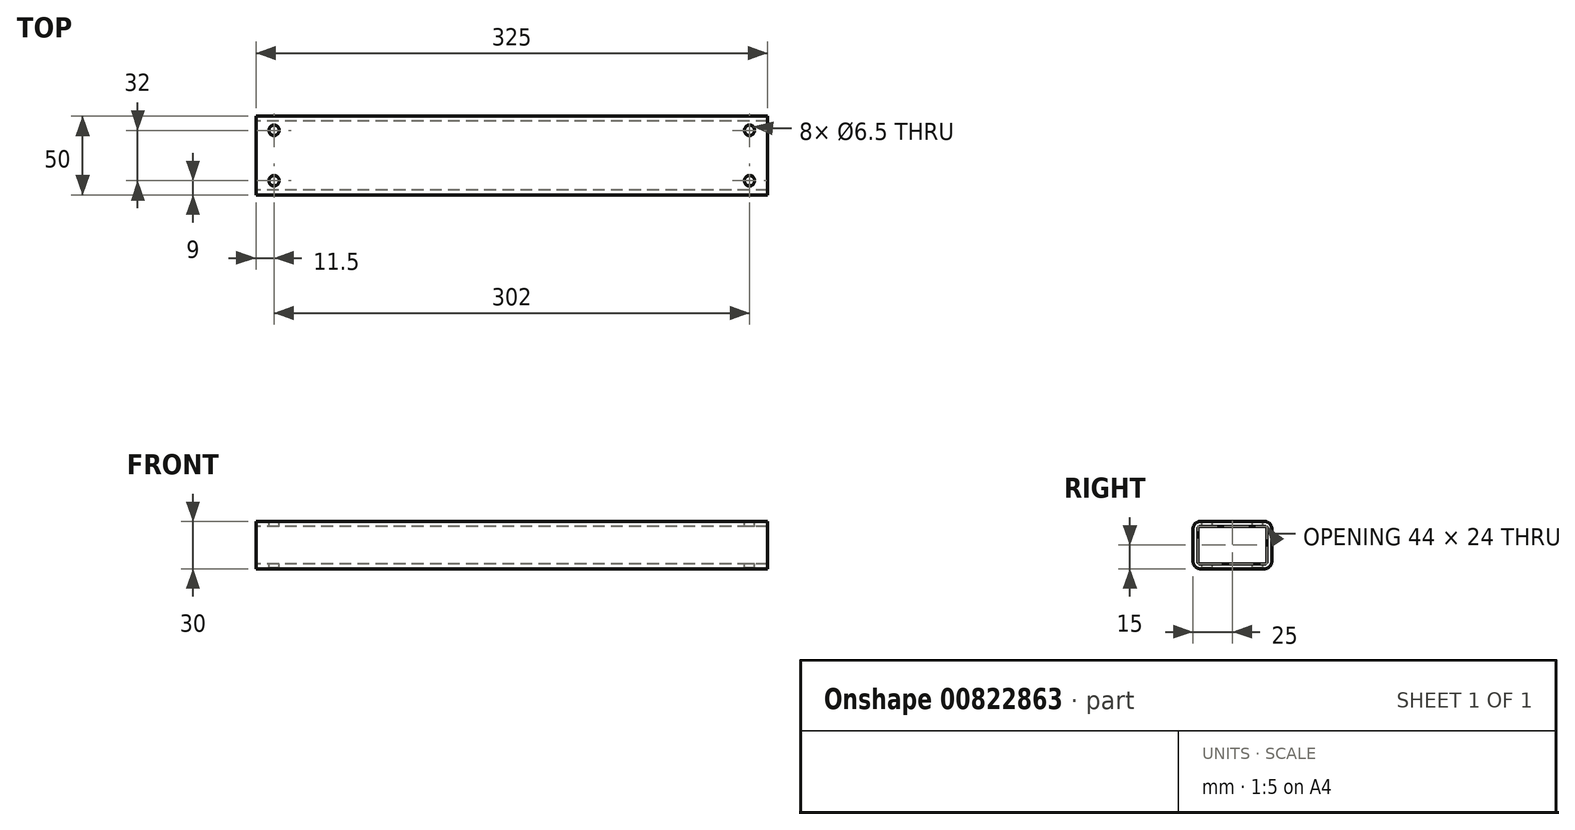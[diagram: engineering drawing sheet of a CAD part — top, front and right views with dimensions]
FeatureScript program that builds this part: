
annotation { "Feature Type Name" : "Feature", "Feature Type Description" : "" }
export const myFeature = defineFeature(function(context is Context, id is Id, definition is map)
    precondition{}
    {
        {
            var Q0;
            Q0=qCreatedBy(makeId("Right.planeOp"),FACE);
            var sketch = newSketch(context, id + "F0", { "sketchPlane" : qUnion([Q0])});
            skLineSegment(sketch, "E0.bottom", {"start": v(-25, -15) * mm, "end": v(25, -15) * mm});
            skLineSegment(sketch, "E0.top", {"start": v(-25, 15) * mm, "end": v(25, 15) * mm});
            skLineSegment(sketch, "E0.left", {"start": v(-25, -15) * mm, "end": v(-25, 15) * mm});
            skLineSegment(sketch, "E0.right", {"start": v(25, -15) * mm, "end": v(25, 15) * mm});
            skPoint(sketch, "E0.middle", {"position": v(0, 0) * mm});
            skLineSegment(sketch, "E1.0", {"start": v(-22, 12) * mm, "end": v(22, 12) * mm});
            skLineSegment(sketch, "E1.1", {"start": v(-22, -12) * mm, "end": v(-22, 12) * mm});
            skLineSegment(sketch, "E1.2", {"start": v(-22, -12) * mm, "end": v(22, -12) * mm});
            skLineSegment(sketch, "E1.3", {"start": v(22, -12) * mm, "end": v(22, 12) * mm});
            skSolve(sketch);
        }
        {
            var Q0;
            Q0=qSketchRegion(id+"F0",true);
            extrude(context, id + "F1", {"entities" : qUnion([Q0]), "endBound" : BoundingType.SYMMETRIC, "depth" : 325 * mm, "offsetDistance" : 25 * mm});
        }
        {
            var Q0;
            Q0=makeQuery(id+"F1.opExtrude","SWEPT_EDGE",EDGE,{"disambiguationData":[OSD([sQuery(id+"F0.wireOp",EDGE,"E1.1"),sQuery(id+"F0.wireOp",EDGE,"E1.2")])]});
            var Q1;
            Q1=makeQuery(id+"F1.opExtrude","SWEPT_EDGE",EDGE,{"disambiguationData":[OSD([sQuery(id+"F0.wireOp",EDGE,"E1.0"),sQuery(id+"F0.wireOp",EDGE,"E1.1")])]});
            var Q2;
            Q2=makeQuery(id+"F1.opExtrude","SWEPT_EDGE",EDGE,{"disambiguationData":[OSD([sQuery(id+"F0.wireOp",EDGE,"E1.2"),sQuery(id+"F0.wireOp",EDGE,"E1.3")])]});
            var Q3;
            Q3=makeQuery(id+"F1.opExtrude","SWEPT_EDGE",EDGE,{"disambiguationData":[OSD([sQuery(id+"F0.wireOp",EDGE,"E1.0"),sQuery(id+"F0.wireOp",EDGE,"E1.3")])]});
            fillet(context, id + "F2", {"entities" : qUnion([Q0, Q1, Q2, Q3]), "radius" : 1.5 * mm, "tangentPropagation" : true, "allowEdgeOverflow" : false});
        }
        {
            var Q0;
            Q0=makeQuery(id+"F1.opExtrude","SWEPT_EDGE",EDGE,{"disambiguationData":[OSD([sQuery(id+"F0.wireOp",EDGE,"E0.top"),sQuery(id+"F0.wireOp",EDGE,"E0.left")])]});
            var Q1;
            Q1=makeQuery(id+"F1.opExtrude","SWEPT_EDGE",EDGE,{"disambiguationData":[OSD([sQuery(id+"F0.wireOp",EDGE,"E0.bottom"),sQuery(id+"F0.wireOp",EDGE,"E0.left")])]});
            var Q2;
            Q2=makeQuery(id+"F1.opExtrude","SWEPT_EDGE",EDGE,{"disambiguationData":[OSD([sQuery(id+"F0.wireOp",EDGE,"E0.bottom"),sQuery(id+"F0.wireOp",EDGE,"E0.right")])]});
            var Q3;
            Q3=makeQuery(id+"F1.opExtrude","SWEPT_EDGE",EDGE,{"disambiguationData":[OSD([sQuery(id+"F0.wireOp",EDGE,"E0.top"),sQuery(id+"F0.wireOp",EDGE,"E0.right")])]});
            fillet(context, id + "F3", {"entities" : qUnion([Q0, Q1, Q2, Q3]), "radius" : 4.5 * mm, "tangentPropagation" : true, "allowEdgeOverflow" : false});
        }
        {
            var Q0;
            Q0=makeQuery(id+"F1.opExtrude","SWEPT_FACE",FACE,{"disambiguationData":[OSD([sQuery(id+"F0.wireOp",EDGE,"E0.top")])]});
            var sketch = newSketch(context, id + "F4", { "sketchPlane" : qUnion([Q0])});
            skLineSegment(sketch, "E2.bottom", {"start": v(-151, 16) * mm, "end": v(151, 16) * mm, "construction": true});
            skLineSegment(sketch, "E2.top", {"start": v(-151, -16) * mm, "end": v(151, -16) * mm, "construction": true});
            skLineSegment(sketch, "E2.left", {"start": v(-151, 16) * mm, "end": v(-151, -16) * mm, "construction": true});
            skLineSegment(sketch, "E2.right", {"start": v(151, 16) * mm, "end": v(151, -16) * mm, "construction": true});
            skPoint(sketch, "E2.middle", {"position": v(0, 0) * mm});
            skCircle(sketch, "E3", {"center": v(-151, 16) * mm, "radius": 3.25 * mm});
            skCircle(sketch, "E4", {"center": v(-151, -16) * mm, "radius": 3.25 * mm});
            skCircle(sketch, "E5", {"center": v(151, -16) * mm, "radius": 3.25 * mm});
            skCircle(sketch, "E6", {"center": v(151, 16) * mm, "radius": 3.25 * mm});
            skSolve(sketch);
        }
        {
            var Q0;
            Q0 = qSketchRegion(id + "F4", true);
            extrude(context, id + "F5", {"entities" : qUnion([Q0]), "operationType" : NewBodyOperationType.REMOVE, "oppositeDirection" : true, "depth" : 35 * mm, "offsetDistance" : 25 * mm});
        }
        {
            var Q0;
            Q0=makeQuery(id+"F5.boolean.opBoolean","COPY",EDGE,{"derivedFrom":makeQuery(id+"F5.opExtrude","CAP_EDGE",EDGE,{"disambiguationData":[OSD([sQuery(id+"F4.wireOp",EDGE,"E4")])],"isStart":true})});
            var Q1;
            Q1=makeQuery(id+"F5.boolean.opBoolean","COPY",EDGE,{"derivedFrom":makeQuery(id+"F5.opExtrude","CAP_EDGE",EDGE,{"disambiguationData":[OSD([sQuery(id+"F4.wireOp",EDGE,"E3")])],"isStart":true})});
            var Q2;
            Q2=makeQuery(id+"F5.boolean.opBoolean","COPY",EDGE,{"derivedFrom":makeQuery(id+"F5.opExtrude","CAP_EDGE",EDGE,{"disambiguationData":[OSD([sQuery(id+"F4.wireOp",EDGE,"E5")])],"isStart":true})});
            var Q3;
            Q3=makeQuery(id+"F5.boolean.opBoolean","COPY",EDGE,{"derivedFrom":makeQuery(id+"F5.opExtrude","CAP_EDGE",EDGE,{"disambiguationData":[OSD([sQuery(id+"F4.wireOp",EDGE,"E6")])],"isStart":true})});
            var Q4;
            Q4=makeQuery(id+"F5.boolean.opBoolean","INTERSECT",EDGE,{"derivedFrom":[makeQuery(id+"F1.opExtrude","SWEPT_FACE",FACE,{"disambiguationData":[OSD([sQuery(id+"F0.wireOp",EDGE,"E0.bottom")])]}),makeQuery(id+"F5.opExtrude","SWEPT_FACE",FACE,{"disambiguationData":[OSD([sQuery(id+"F4.wireOp",EDGE,"E6")])]})]});
            var Q5;
            Q5=makeQuery(id+"F5.boolean.opBoolean","INTERSECT",EDGE,{"derivedFrom":[makeQuery(id+"F1.opExtrude","SWEPT_FACE",FACE,{"disambiguationData":[OSD([sQuery(id+"F0.wireOp",EDGE,"E0.bottom")])]}),makeQuery(id+"F5.opExtrude","SWEPT_FACE",FACE,{"disambiguationData":[OSD([sQuery(id+"F4.wireOp",EDGE,"E5")])]})]});
            var Q6;
            Q6=makeQuery(id+"F5.boolean.opBoolean","INTERSECT",EDGE,{"derivedFrom":[makeQuery(id+"F1.opExtrude","SWEPT_FACE",FACE,{"disambiguationData":[OSD([sQuery(id+"F0.wireOp",EDGE,"E0.bottom")])]}),makeQuery(id+"F5.opExtrude","SWEPT_FACE",FACE,{"disambiguationData":[OSD([sQuery(id+"F4.wireOp",EDGE,"E3")])]})]});
            var Q7;
            Q7=makeQuery(id+"F5.boolean.opBoolean","INTERSECT",EDGE,{"derivedFrom":[makeQuery(id+"F1.opExtrude","SWEPT_FACE",FACE,{"disambiguationData":[OSD([sQuery(id+"F0.wireOp",EDGE,"E0.bottom")])]}),makeQuery(id+"F5.opExtrude","SWEPT_FACE",FACE,{"disambiguationData":[OSD([sQuery(id+"F4.wireOp",EDGE,"E4")])]})]});
            chamfer(context, id + "F6", {"entities" : qUnion([Q0, Q1, Q2, Q3, Q4, Q5, Q6, Q7]), "width" : 0.5 * mm, "tangentPropagation" : true});
        }
    });
